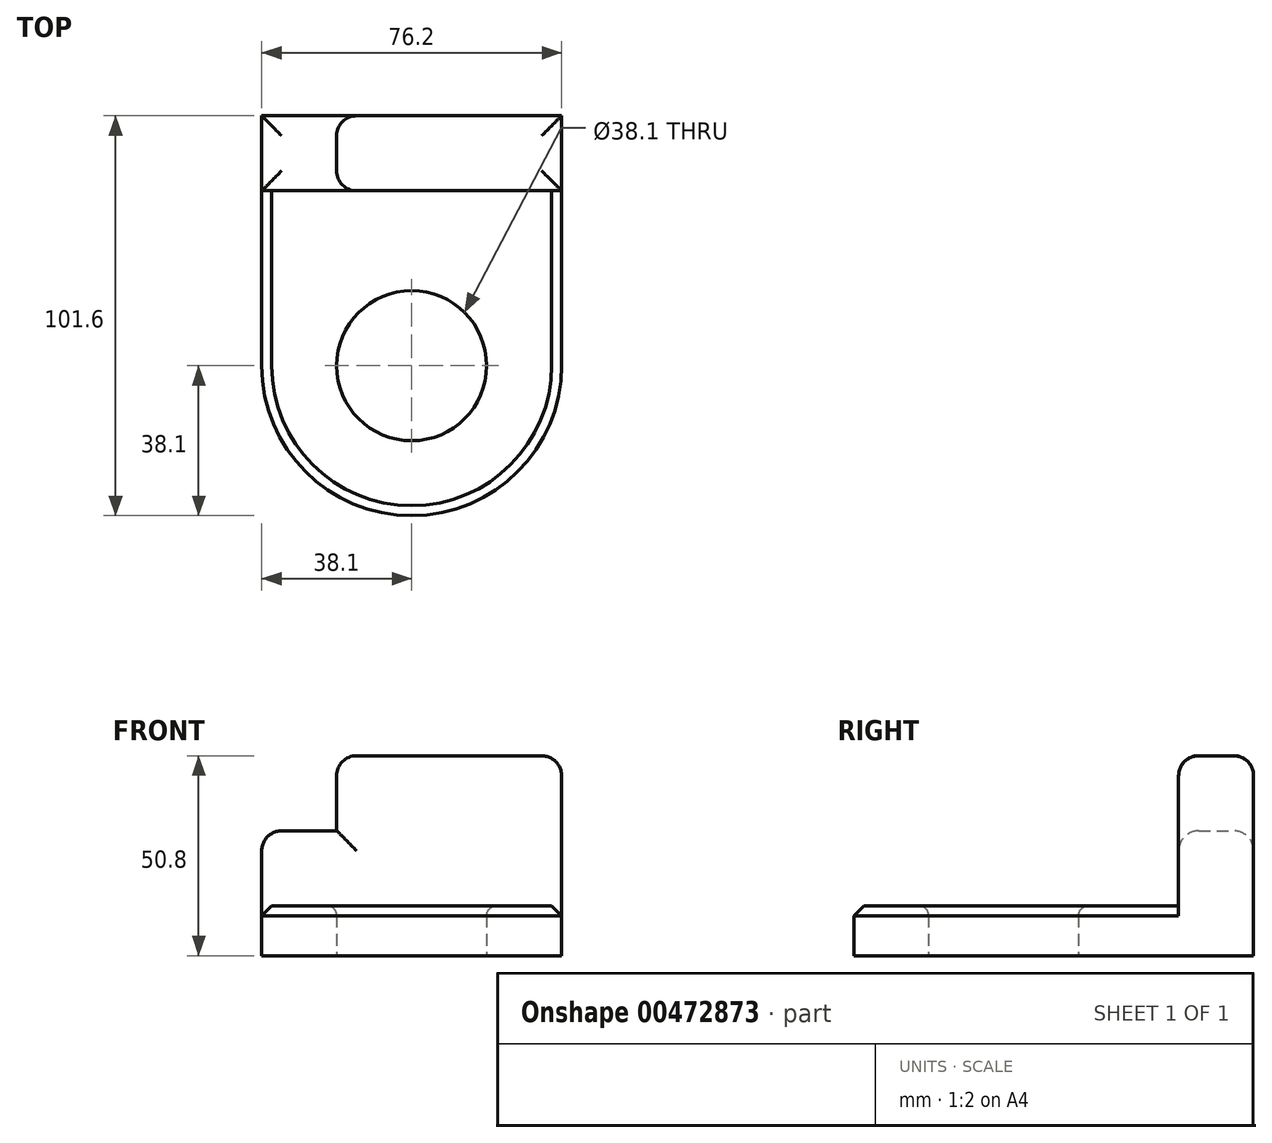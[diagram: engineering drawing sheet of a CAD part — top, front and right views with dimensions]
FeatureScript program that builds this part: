
annotation { "Feature Type Name" : "Feature", "Feature Type Description" : "" }
export const myFeature = defineFeature(function(context is Context, id is Id, definition is map)
    precondition{}
    {
        {
            var Q0;
            Q0=qCreatedBy(makeId("Front.planeOp"),FACE);
            var sketch = newSketch(context, id + "F0", { "sketchPlane" : qUnion([Q0])});
            skLineSegment(sketch, "E0.bottom", {"start": v(0, 0) * mm, "end": v(38.1, 0) * mm});
            skLineSegment(sketch, "E0.top", {"start": v(0, 12.7) * mm, "end": v(38.1, 12.7) * mm});
            skLineSegment(sketch, "E0.left", {"start": v(0, 0) * mm, "end": v(0, 12.7) * mm});
            skLineSegment(sketch, "E0.right", {"start": v(38.1, 0) * mm, "end": v(38.1, 12.7) * mm});
            skSolve(sketch);
        }
        {
            var Q0;
            Q0=makeQuery(id+"F0.imprint","IMPRINT",FACE,{"disambiguationData":[TD([[makeQuery(id+"F0.imprint","IMPRINT",EDGE,{"derivedFrom":sQuery(id+"F0.wireOp",EDGE,"E0.bottom")}),1.0]])]});
            var Q1;
            Q1=sQuery(id+"F0.wireOp",EDGE,"E0.left");
            revolve(context, id + "F1", {"entities" : qUnion([Q0]), "axis" : qUnion([Q1]), "revolveType" : RevolveType.FULL});
        }
        {
            var Q0;
            Q0=qCreatedBy(makeId("Right.planeOp"),FACE);
            var sketch = newSketch(context, id + "F2", { "sketchPlane" : qUnion([Q0])});
            skLineSegment(sketch, "E1.bottom", {"start": v(0, 0) * mm, "end": v(63.5, 0) * mm});
            skLineSegment(sketch, "E1.top", {"start": v(0, 12.7) * mm, "end": v(63.5, 12.7) * mm});
            skLineSegment(sketch, "E1.left", {"start": v(0, 0) * mm, "end": v(0, 12.7) * mm});
            skLineSegment(sketch, "E1.right", {"start": v(63.5, 0) * mm, "end": v(63.5, 12.7) * mm});
            skSolve(sketch);
        }
        {
            var Q0;
            Q0=makeQuery(id+"F2.imprint","IMPRINT",FACE,{"disambiguationData":[TD([[makeQuery(id+"F2.imprint","IMPRINT",EDGE,{"derivedFrom":sQuery(id+"F2.wireOp",EDGE,"E1.bottom")}),1.0]])]});
            extrude(context, id + "F3", {"entities" : qUnion([Q0]), "operationType" : NewBodyOperationType.ADD, "endBound" : BoundingType.SYMMETRIC, "depth" : 76.2 * mm});
        }
        {
            var Q0;
            Q0=qCreatedBy(makeId("Top.planeOp"),FACE);
            var sketch = newSketch(context, id + "F4", { "sketchPlane" : qUnion([Q0])});
            skCircle(sketch, "E2", {"center": v(0, 0) * mm, "radius": 19.05 * mm});
            skSolve(sketch);
        }
        {
            var Q0;
            Q0 = qSketchRegion(id + "F4", true);
            extrude(context, id + "F5", {"entities" : qUnion([Q0]), "operationType" : NewBodyOperationType.REMOVE, "endBound" : BoundingType.THROUGH_ALL, "depth" : 25.9 * mm});
        }
        {
            var Q0;
            Q0=qCreatedBy(makeId("Right.planeOp"),FACE);
            var sketch = newSketch(context, id + "F6", { "sketchPlane" : qUnion([Q0])});
            skLineSegment(sketch, "E3.bottom", {"start": v(44.45, 31.75) * mm, "end": v(63.5, 31.75) * mm});
            skLineSegment(sketch, "E3.top", {"start": v(44.45, 12.7) * mm, "end": v(63.5, 12.7) * mm});
            skLineSegment(sketch, "E3.left", {"start": v(44.45, 31.75) * mm, "end": v(44.45, 12.7) * mm});
            skLineSegment(sketch, "E3.right", {"start": v(63.5, 31.75) * mm, "end": v(63.5, 12.7) * mm});
            skPoint(sketch, "E3.middle", {"position": v(53.98, 22.23) * mm});
            skSolve(sketch);
        }
        {
            var Q0;
            Q0=makeQuery(id+"F6.imprint","IMPRINT",FACE,{"disambiguationData":[TD([[makeQuery(id+"F6.imprint","IMPRINT",EDGE,{"derivedFrom":sQuery(id+"F6.wireOp",EDGE,"E3.bottom")}),-1.0]])]});
            extrude(context, id + "F7", {"entities" : qUnion([Q0]), "operationType" : NewBodyOperationType.ADD, "endBound" : BoundingType.SYMMETRIC, "depth" : 76.2 * mm});
        }
        {
            var Q0;
            Q0=qCreatedBy(makeId("Right.planeOp"),FACE);
            var sketch = newSketch(context, id + "F8", { "sketchPlane" : qUnion([Q0])});
            skLineSegment(sketch, "E4.bottom", {"start": v(44.45, 31.75) * mm, "end": v(63.5, 31.75) * mm});
            skLineSegment(sketch, "E4.top", {"start": v(44.45, 50.8) * mm, "end": v(63.5, 50.8) * mm});
            skLineSegment(sketch, "E4.left", {"start": v(44.45, 31.75) * mm, "end": v(44.45, 50.8) * mm});
            skLineSegment(sketch, "E4.right", {"start": v(63.5, 31.75) * mm, "end": v(63.5, 50.8) * mm});
            skSolve(sketch);
        }
        {
            var Q0;
            Q0=makeQuery(id+"F8.imprint","IMPRINT",FACE,{"disambiguationData":[TD([[makeQuery(id+"F8.imprint","IMPRINT",EDGE,{"derivedFrom":sQuery(id+"F8.wireOp",EDGE,"E4.bottom")}),1.0]])]});
            extrude(context, id + "F9", {"entities" : qUnion([Q0]), "operationType" : NewBodyOperationType.ADD, "depth" : 38.1 * mm});
        }
        {
            var Q0;
            Q0=makeQuery(id+"F9.opExtrude","CAP_FACE",FACE,{"disambiguationData":[OSD([sQuery(id+"F8.wireOp",EDGE,"E4.bottom"),sQuery(id+"F8.wireOp",EDGE,"E4.top"),sQuery(id+"F8.wireOp",EDGE,"E4.left"),sQuery(id+"F8.wireOp",EDGE,"E4.right")])],"isStart":true});
            extrude(context, id + "F10", {"entities" : qUnion([Q0]), "operationType" : NewBodyOperationType.ADD, "depth" : 19.05 * mm});
        }
        {
            var Q0;
            Q0=makeQuery(id+"F5.boolean.opBoolean","INTERSECT",EDGE,{"derivedFrom":[makeQuery(id+"F3.boolean.opBoolean","MERGE",FACE,{"derivedFrom":[makeQuery(id+"F1.opRevolve","SWEPT_FACE",FACE,{"disambiguationData":[OSD([sQuery(id+"F0.wireOp",EDGE,"E0.top")])]}),makeQuery(id+"F3.opExtrude","SWEPT_FACE",FACE,{"disambiguationData":[OSD([sQuery(id+"F2.wireOp",EDGE,"E1.top")])]})]}),makeQuery(id+"F5.opExtrude","SWEPT_FACE",FACE,{"disambiguationData":[OSD([sQuery(id+"F4.wireOp",EDGE,"E2")])]})]});
            var Q1;
            Q1=makeQuery(id+"F5.boolean.opBoolean","COPY",EDGE,{"derivedFrom":makeQuery(id+"F5.opExtrude","CAP_EDGE",EDGE,{"disambiguationData":[OSD([sQuery(id+"F4.wireOp",EDGE,"E2")])],"isStart":true})});
            var Q2;
            Q2=makeQuery(id+"F7.opExtrude","SWEPT_EDGE",EDGE,{"disambiguationData":[OSD([sQuery(id+"F6.wireOp",EDGE,"E3.top"),sQuery(id+"F6.wireOp",EDGE,"E3.left")])]});
            fillet(context, id + "F11", {"entities" : qUnion([Q0, Q1, Q2]), "radius" : 2.54 * mm, "tangentPropagation" : true, "allowEdgeOverflow" : false});
        }
        {
            var Q0;
            Q0=makeQuery(id+"F3.opExtrude","CAP_EDGE",EDGE,{"disambiguationData":[OSD([sQuery(id+"F2.wireOp",EDGE,"E1.top")])],"isStart":false});
            var Q1;
            Q1=makeQuery(id+"F1.opRevolve","SWEPT_EDGE",EDGE,{"disambiguationData":[OSD([sQuery(id+"F0.wireOp",EDGE,"E0.top"),sQuery(id+"F0.wireOp",EDGE,"E0.right")])]});
            var Q2;
            Q2=makeQuery(id+"F10.opExtrude","CAP_EDGE",EDGE,{"disambiguationData":[OSD([sQuery(id+"F8.wireOp",EDGE,"E4.bottom")])],"isStart":false});
            chamfer(context, id + "F12", {"entities" : qUnion([Q0, Q1, Q2]), "width" : 2.54 * mm, "tangentPropagation" : true});
        }
        {
            var Q0;
            Q0=makeQuery(id+"F9.opExtrude","CAP_EDGE",EDGE,{"disambiguationData":[OSD([sQuery(id+"F8.wireOp",EDGE,"E4.top")])],"isStart":false});
            var Q1;
            {var subQ0=sQuery(id+"F8.wireOp",EDGE,"E4.left");var subQ1=sQuery(id+"F8.wireOp",EDGE,"E4.top");Q1=makeQuery(id+"F10.boolean.opBoolean","MERGE",EDGE,{"derivedFrom":[makeQuery(id+"F9.opExtrude","SWEPT_EDGE",EDGE,{"disambiguationData":[OSD([subQ1,subQ0])]}),makeQuery(id+"F10.opExtrude","SWEPT_EDGE",EDGE,{"disambiguationData":[OSD([subQ1,subQ0])]})]});}
            var Q2;
            {var subQ0=sQuery(id+"F8.wireOp",EDGE,"E4.top");Q2=makeQuery(id+"F12.opChamfer","BLEND_EDGE",EDGE,{"blendedFrom":[makeQuery(id+"F9.boolean.opBoolean","MERGE",EDGE,{"derivedFrom":[makeQuery(id+"F7.opExtrude","CAP_EDGE",EDGE,{"disambiguationData":[OSD([sQuery(id+"F6.wireOp",EDGE,"E3.left")])],"isStart":false}),makeQuery(id+"F9.opExtrude","CAP_EDGE",EDGE,{"disambiguationData":[OSD([sQuery(id+"F8.wireOp",EDGE,"E4.left")])],"isStart":false})]}),makeQuery(id+"F10.boolean.opBoolean","MERGE",FACE,{"derivedFrom":[makeQuery(id+"F9.opExtrude","SWEPT_FACE",FACE,{"disambiguationData":[OSD([subQ0])]}),makeQuery(id+"F10.opExtrude","SWEPT_FACE",FACE,{"disambiguationData":[OSD([subQ0])]})]})],"blendedInto":[makeQuery(id+"F10.boolean.opBoolean","MERGE",FACE,{"derivedFrom":[makeQuery(id+"F9.opExtrude","SWEPT_FACE",FACE,{"disambiguationData":[OSD([subQ0])]}),makeQuery(id+"F10.opExtrude","SWEPT_FACE",FACE,{"disambiguationData":[OSD([subQ0])]})]})]});}
            var Q3;
            Q3=makeQuery(id+"F10.opExtrude","CAP_EDGE",EDGE,{"disambiguationData":[OSD([sQuery(id+"F8.wireOp",EDGE,"E4.top")])],"isStart":false});
            var Q4;
            {var subQ0=sQuery(id+"F8.wireOp",EDGE,"E4.right");var subQ1=sQuery(id+"F8.wireOp",EDGE,"E4.top");Q4=makeQuery(id+"F10.boolean.opBoolean","MERGE",EDGE,{"derivedFrom":[makeQuery(id+"F9.opExtrude","SWEPT_EDGE",EDGE,{"disambiguationData":[OSD([subQ1,subQ0])]}),makeQuery(id+"F10.opExtrude","SWEPT_EDGE",EDGE,{"disambiguationData":[OSD([subQ1,subQ0])]})]});}
            var Q5;
            Q5=makeQuery(id+"F7.opExtrude","SWEPT_EDGE",EDGE,{"disambiguationData":[OSD([sQuery(id+"F6.wireOp",EDGE,"E3.bottom"),sQuery(id+"F6.wireOp",EDGE,"E3.right")])]});
            var Q6;
            Q6=makeQuery(id+"F10.opExtrude","CAP_EDGE",EDGE,{"disambiguationData":[OSD([sQuery(id+"F8.wireOp",EDGE,"E4.right")])],"isStart":false});
            var Q7;
            {var subQ0=sQuery(id+"F8.wireOp",EDGE,"E4.right");Q7=makeQuery(id+"F12.opChamfer","BLEND_EDGE",EDGE,{"blendedFrom":[makeQuery(id+"F10.opExtrude","CAP_EDGE",EDGE,{"disambiguationData":[OSD([sQuery(id+"F8.wireOp",EDGE,"E4.bottom")])],"isStart":false}),makeQuery(id+"F10.boolean.opBoolean","MERGE",FACE,{"derivedFrom":[makeQuery(id+"F9.boolean.opBoolean","MERGE",FACE,{"derivedFrom":[makeQuery(id+"F7.boolean.opBoolean","MERGE",FACE,{"derivedFrom":[makeQuery(id+"F3.opExtrude","SWEPT_FACE",FACE,{"disambiguationData":[OSD([sQuery(id+"F2.wireOp",EDGE,"E1.right")])]}),makeQuery(id+"F7.opExtrude","SWEPT_FACE",FACE,{"disambiguationData":[OSD([sQuery(id+"F6.wireOp",EDGE,"E3.right")])]})]}),makeQuery(id+"F9.opExtrude","SWEPT_FACE",FACE,{"disambiguationData":[OSD([subQ0])]})]}),makeQuery(id+"F10.opExtrude","SWEPT_FACE",FACE,{"disambiguationData":[OSD([subQ0])]})]})],"blendedInto":[makeQuery(id+"F10.boolean.opBoolean","MERGE",FACE,{"derivedFrom":[makeQuery(id+"F9.boolean.opBoolean","MERGE",FACE,{"derivedFrom":[makeQuery(id+"F7.boolean.opBoolean","MERGE",FACE,{"derivedFrom":[makeQuery(id+"F3.opExtrude","SWEPT_FACE",FACE,{"disambiguationData":[OSD([sQuery(id+"F2.wireOp",EDGE,"E1.right")])]}),makeQuery(id+"F7.opExtrude","SWEPT_FACE",FACE,{"disambiguationData":[OSD([sQuery(id+"F6.wireOp",EDGE,"E3.right")])]})]}),makeQuery(id+"F9.opExtrude","SWEPT_FACE",FACE,{"disambiguationData":[OSD([subQ0])]})]}),makeQuery(id+"F10.opExtrude","SWEPT_FACE",FACE,{"disambiguationData":[OSD([subQ0])]})]})]});}
            var Q8;
            Q8=makeQuery(id+"F7.opExtrude","CAP_EDGE",EDGE,{"disambiguationData":[OSD([sQuery(id+"F6.wireOp",EDGE,"E3.bottom")])],"isStart":true});
            var Q9;
            Q9=makeQuery(id+"F7.opExtrude","SWEPT_EDGE",EDGE,{"disambiguationData":[OSD([sQuery(id+"F6.wireOp",EDGE,"E3.bottom"),sQuery(id+"F6.wireOp",EDGE,"E3.left")])]});
            var Q10;
            {var subQ0=sQuery(id+"F8.wireOp",EDGE,"E4.left");Q10=makeQuery(id+"F12.opChamfer","BLEND_EDGE",EDGE,{"blendedFrom":[makeQuery(id+"F10.opExtrude","CAP_EDGE",EDGE,{"disambiguationData":[OSD([sQuery(id+"F8.wireOp",EDGE,"E4.bottom")])],"isStart":false}),makeQuery(id+"F10.boolean.opBoolean","MERGE",FACE,{"derivedFrom":[makeQuery(id+"F9.boolean.opBoolean","MERGE",FACE,{"derivedFrom":[makeQuery(id+"F7.opExtrude","SWEPT_FACE",FACE,{"disambiguationData":[OSD([sQuery(id+"F6.wireOp",EDGE,"E3.left")])]}),makeQuery(id+"F9.opExtrude","SWEPT_FACE",FACE,{"disambiguationData":[OSD([subQ0])]})]}),makeQuery(id+"F10.opExtrude","SWEPT_FACE",FACE,{"disambiguationData":[OSD([subQ0])]})]})],"blendedInto":[makeQuery(id+"F10.boolean.opBoolean","MERGE",FACE,{"derivedFrom":[makeQuery(id+"F9.boolean.opBoolean","MERGE",FACE,{"derivedFrom":[makeQuery(id+"F7.opExtrude","SWEPT_FACE",FACE,{"disambiguationData":[OSD([sQuery(id+"F6.wireOp",EDGE,"E3.left")])]}),makeQuery(id+"F9.opExtrude","SWEPT_FACE",FACE,{"disambiguationData":[OSD([subQ0])]})]}),makeQuery(id+"F10.opExtrude","SWEPT_FACE",FACE,{"disambiguationData":[OSD([subQ0])]})]})]});}
            var Q11;
            Q11=makeQuery(id+"F10.opExtrude","CAP_EDGE",EDGE,{"disambiguationData":[OSD([sQuery(id+"F8.wireOp",EDGE,"E4.left")])],"isStart":false});
            fillet(context, id + "F13", {"entities" : qUnion([Q0, Q1, Q2, Q3, Q4, Q5, Q6, Q7, Q8, Q9, Q10, Q11]), "radius" : 5.08 * mm, "tangentPropagation" : true, "allowEdgeOverflow" : false});
        }
    });
